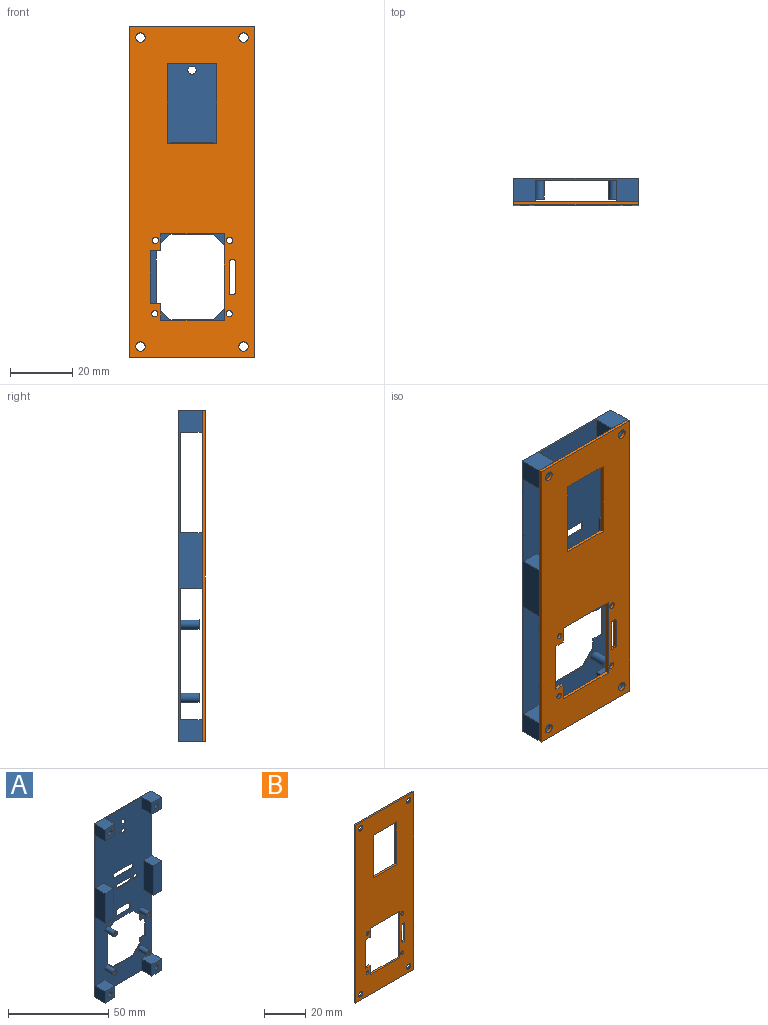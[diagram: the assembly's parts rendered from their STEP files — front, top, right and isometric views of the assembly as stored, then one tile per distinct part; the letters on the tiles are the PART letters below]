
ASSEMBLY  parts=2 mates=1
PART A: 73 faces, bbox 40x7.5x106 mm
  f0: plane 106x40mm, normal (0,-1,0), area 3029.2mm2, adj f1,f2,f3,f4,f5,f6,f7,f8
  f1: plane 9.53x0.5mm, normal (0,0,1), area 4.8mm2, adj f0,f2,f27,f40
  f2: plane 4x0.5mm, normal (1,0,0), area 2mm2, adj f0,f1,f3,f40
  f3: plane 9.53x0.5mm, normal (0,0,-1), area 4.8mm2, adj f0,f2,f27,f40
  f4: plane 40x7.5mm, normal (0,0,1), area 118mm2, adj f0,f5,f33,f40,f50,f51,f53,f54
  f5: plane 106x7.5mm, normal (-1,0,0), area 277mm2, adj f0,f4,f6,f40,f52,f54,f59,f60
  f6: plane 40x7.5mm, normal (0,0,-1), area 118mm2, adj f0,f5,f33,f40,f56,f57,f58,f60
  f7: plane 2.7x0.5mm, normal (0,0,1), area 1.3mm2, adj f0,f8,f34,f40
  f8: plane 2.75x0.5mm, normal (1,0,0), area 1.4mm2, adj f0,f7,f9,f40
  f9: plane 2.7x0.5mm, normal (0,0,-1), area 1.3mm2, adj f0,f8,f34,f40
  f10: plane 18.65x0.5mm, normal (1,0,0), area 9.3mm2, adj f0,f11,f35,f40
  f11: plane 4.42x4.42mm, normal (0.71,0,-0.71), area 3.1mm2, adj f0,f10,f12,f40
  f12: plane 13.95x0.5mm, normal (0,0,-1), area 7mm2, adj f0,f11,f13,f40
  f13: plane 5x5mm, normal (-0.71,0,-0.71), area 3.5mm2, adj f0,f12,f14,f40
  f14: plane 3.25x0.5mm, normal (-1,0,0), area 1.6mm2, adj f0,f13,f15,f40
  f15: plane 3.77x0.5mm, normal (0,0,-1), area 1.9mm2, adj f0,f14,f16,f40
  f16: plane 11x0.5mm, normal (-1,0,0), area 5.5mm2, adj f0,f15,f17,f40
  f17: plane 3.77x0.5mm, normal (0,0,1), area 1.9mm2, adj f0,f16,f18,f40
  f18: plane 3.25x0.5mm, normal (-1,0,0), area 1.6mm2, adj f0,f17,f19,f40
  f19: plane 5x5mm, normal (-0.71,0,0.71), area 3.5mm2, adj f0,f18,f20,f40
  f20: plane 13.95x0.5mm, normal (0,0,1), area 7mm2, adj f0,f19,f35,f40
  f21: plane 13.8x0.5mm, normal (0,0,1), area 6.9mm2, adj f0,f22,f36,f40
  f22: plane 3x0.5mm, normal (1,0,0), area 1.5mm2, adj f0,f21,f23,f40
  f23: plane 13.8x0.5mm, normal (0,0,-1), area 6.9mm2, adj f0,f22,f36,f40
  f24: plane 2.4x0.5mm, normal (-1,0,0), area 1.2mm2, adj f0,f25,f37,f40
  f25: plane 10x0.5mm, normal (0,0,1), area 5mm2, adj f0,f24,f26,f40
  f26: plane 2.4x0.5mm, normal (1,0,0), area 1.2mm2, adj f0,f25,f37,f40
  f27: plane 4x0.5mm, normal (-1,0,0), area 2mm2, adj f0,f1,f3,f40
  f28: cylinder r=1.35mm len=2.7mm, axis (0,1,0), area 4.2mm2, adj f0,f40
  f29: cylinder r=1mm len=6.5mm, axis (0,1,0), area 40.8mm2, adj f40,f44
  f30: cylinder r=1mm len=6.5mm, axis (0,1,0), area 40.8mm2, adj f40,f48
  f31: cylinder r=1mm len=6.5mm, axis (0,1,0), area 40.8mm2, adj f40,f42
  f32: cylinder r=1mm len=6.5mm, axis (0,1,0), area 40.8mm2, adj f40,f46
  f33: plane 106x7.5mm, normal (1,0,0), area 277mm2, adj f0,f4,f6,f40,f49,f51,f55,f57
  f34: plane 2.75x0.5mm, normal (-1,0,0), area 1.4mm2, adj f0,f7,f9,f40
  f35: plane 4.42x4.42mm, normal (0.71,0,0.71), area 3.1mm2, adj f0,f10,f20,f40
  f36: plane 3x0.5mm, normal (-1,0,0), area 1.5mm2, adj f0,f21,f23,f40
  f37: plane 10x0.5mm, normal (0,0,-1), area 5mm2, adj f0,f24,f26,f40
  f38: cylinder r=1.5mm len=3mm, axis (0,1,0), area 4.7mm2, adj f0,f40
  f39: cylinder r=1.5mm len=3mm, axis (0,1,0), area 4.7mm2, adj f0,f40
  f40: plane 106x40mm, normal (0,1,0), area 3428.6mm2, adj f1,f2,f3,f4,f5,f6,f7,f8
  f41: cylinder r=1.5mm len=6mm, axis (0,1,0), area 56.5mm2, adj f0,f42
  f42: plane 3x3mm, normal (0,-1,0), area 3.9mm2, adj f31,f41
  f43: cylinder r=1.5mm len=6mm, axis (0,1,0), area 56.5mm2, adj f0,f44
  f44: plane 3x3mm, normal (0,-1,0), area 3.9mm2, adj f29,f43
  f45: cylinder r=1.5mm len=6mm, axis (0,1,0), area 56.5mm2, adj f0,f46
  f46: plane 3x3mm, normal (0,-1,0), area 3.9mm2, adj f32,f45
  f47: cylinder r=1.5mm len=6mm, axis (0,1,0), area 56.5mm2, adj f0,f48
  f48: plane 3x3mm, normal (0,-1,0), area 3.9mm2, adj f30,f47
  f49: plane 7x7mm, normal (0,0,-1), area 49mm2, adj f0,f33,f50,f51
  f50: plane 7x7mm, normal (-1,0,0), area 49mm2, adj f0,f4,f49,f51
  f51: plane 7x7mm, normal (0,-1,0), area 41.9mm2, adj f4,f33,f49,f50,f72
  f52: plane 7x7mm, normal (0,0,-1), area 49mm2, adj f0,f5,f53,f54
  f53: plane 7x7mm, normal (1,0,0), area 49mm2, adj f0,f4,f52,f54
  f54: plane 7x7mm, normal (0,-1,0), area 41.9mm2, adj f4,f5,f52,f53,f71
  f55: plane 7x7mm, normal (0,0,1), area 49mm2, adj f0,f33,f56,f57
  f56: plane 7x7mm, normal (-1,0,0), area 49mm2, adj f0,f6,f55,f57
  f57: plane 7x7mm, normal (0,-1,0), area 41.9mm2, adj f6,f33,f55,f56,f70
  f58: plane 7x7mm, normal (1,0,0), area 49mm2, adj f0,f6,f59,f60
  f59: plane 7x7mm, normal (0,0,1), area 49mm2, adj f0,f5,f58,f60
  f60: plane 7x7mm, normal (0,-1,0), area 41.9mm2, adj f5,f6,f58,f59,f69
  f61: plane 7x6mm, normal (0,0,-1), area 42mm2, adj f0,f33,f63,f64
  f62: plane 7x6mm, normal (0,0,1), area 42mm2, adj f0,f33,f63,f64
  f63: plane 18x7mm, normal (-1,0,0), area 126mm2, adj f0,f61,f62,f64
  f64: plane 18x6mm, normal (0,-1,0), area 108mm2, adj f33,f61,f62,f63
  f65: plane 7x6mm, normal (0,0,-1), area 42mm2, adj f0,f5,f66,f68
  f66: plane 18x7mm, normal (1,0,0), area 126mm2, adj f0,f65,f67,f68
  f67: plane 7x6mm, normal (0,0,1), area 42mm2, adj f0,f5,f66,f68
  f68: plane 18x6mm, normal (0,-1,0), area 108mm2, adj f5,f65,f66,f67
  f69: cylinder r=1.5mm len=7.5mm, axis (0,-1,0), area 70.7mm2, adj f40,f60
  f70: cylinder r=1.5mm len=7.5mm, axis (0,-1,0), area 70.7mm2, adj f40,f57
  f71: cylinder r=1.5mm len=7.5mm, axis (0,-1,0), area 70.7mm2, adj f40,f54
  f72: cylinder r=1.5mm len=7.5mm, axis (0,-1,0), area 70.7mm2, adj f40,f51
PART B: 34 faces, bbox 40x1x106 mm
  f0: plane 1x0.98mm, normal (0,0,-1), area 1mm2, adj f27,f28,f30,f31
  f1: plane 16x1mm, normal (0,0,-1), area 16mm2, adj f2,f26,f27,f28
  f2: plane 25.5x1mm, normal (-1,0,0), area 25.5mm2, adj f1,f3,f27,f28
  f3: plane 16x1mm, normal (0,0,1), area 16mm2, adj f2,f26,f27,f28
  f4: plane 40x1mm, normal (0,0,1), area 40mm2, adj f5,f16,f27,f28
  f5: plane 106x1mm, normal (-1,0,0), area 106mm2, adj f4,f6,f27,f28
  f6: plane 40x1mm, normal (0,0,-1), area 40mm2, adj f5,f16,f27,f28
  f7: plane 10x1mm, normal (-1,0,0), area 10mm2, adj f27,f28,f30,f32
  f8: plane 1x0.98mm, normal (0,0,1), area 1mm2, adj f27,f28,f32,f33
  f9: plane 20.26x1mm, normal (0,0,1), area 20.3mm2, adj f10,f25,f27,f28
  f10: plane 5.4x1mm, normal (1,0,0), area 5.4mm2, adj f9,f11,f27,f28
  f11: plane 3.39x1mm, normal (0,0,1), area 3.4mm2, adj f10,f12,f27,f28
  f12: plane 16.9x1mm, normal (1,0,0), area 16.9mm2, adj f11,f13,f27,f28
  f13: plane 3.39x1mm, normal (0,0,-1), area 3.4mm2, adj f12,f14,f27,f28
  f14: plane 5.4x1mm, normal (1,0,0), area 5.4mm2, adj f13,f15,f27,f28
  f15: plane 20.26x1mm, normal (0,0,-1), area 20.3mm2, adj f14,f25,f27,f28
  f16: plane 106x1mm, normal (1,0,0), area 106mm2, adj f4,f6,f27,f28
  f17: cylinder r=1mm len=2mm, axis (0,1,0), area 6.3mm2, adj f27,f28
  f18: cylinder r=1mm len=2mm, axis (0,1,0), area 6.3mm2, adj f27,f28
  f19: cylinder r=1mm len=2mm, axis (0,1,0), area 6.3mm2, adj f27,f28
  f20: cylinder r=1mm len=2mm, axis (0,1,0), area 6.3mm2, adj f27,f28
  f21: cylinder r=1.5mm len=3mm, axis (0,1,0), area 9.4mm2, adj f27,f28
  f22: cylinder r=1.5mm len=3mm, axis (0,1,0), area 9.4mm2, adj f27,f28
  f23: cylinder r=1.5mm len=3mm, axis (0,1,0), area 9.4mm2, adj f27,f28
  f24: cylinder r=1.5mm len=3mm, axis (0,1,0), area 9.4mm2, adj f27,f28
  f25: plane 27.7x1mm, normal (-1,0,0), area 27.7mm2, adj f9,f15,f27,f28
  f26: plane 25.5x1mm, normal (1,0,0), area 25.5mm2, adj f1,f3,f27,f28
  f27: plane 106x40mm, normal (0,-1,0), area 3151.2mm2, adj f0,f1,f2,f3,f4,f5,f6,f7
  f28: plane 106x40mm, normal (0,1,0), area 3151.2mm2, adj f0,f1,f2,f3,f4,f5,f6,f7
  f29: plane 10x1mm, normal (1,0,0), area 10mm2, adj f27,f28,f31,f33
  f30: cylinder r=0.5mm len=1mm, axis (0,-1,0), area 0.8mm2, adj f0,f7,f27,f28
  f31: cylinder r=0.5mm len=1mm, axis (0,-1,0), area 0.8mm2, adj f0,f27,f28,f29
  f32: cylinder r=0.5mm len=1mm, axis (0,-1,0), area 0.8mm2, adj f7,f8,f27,f28
  f33: cylinder r=0.5mm len=1mm, axis (0,-1,0), area 0.8mm2, adj f8,f27,f28,f29
PLACE A at identity
PLACE B t=(0,-7.5,0.88)mm
MATE slider B.f22 <-> A.f71  axis (0,1,0) through (24.34,-116.5,71.68)mm
